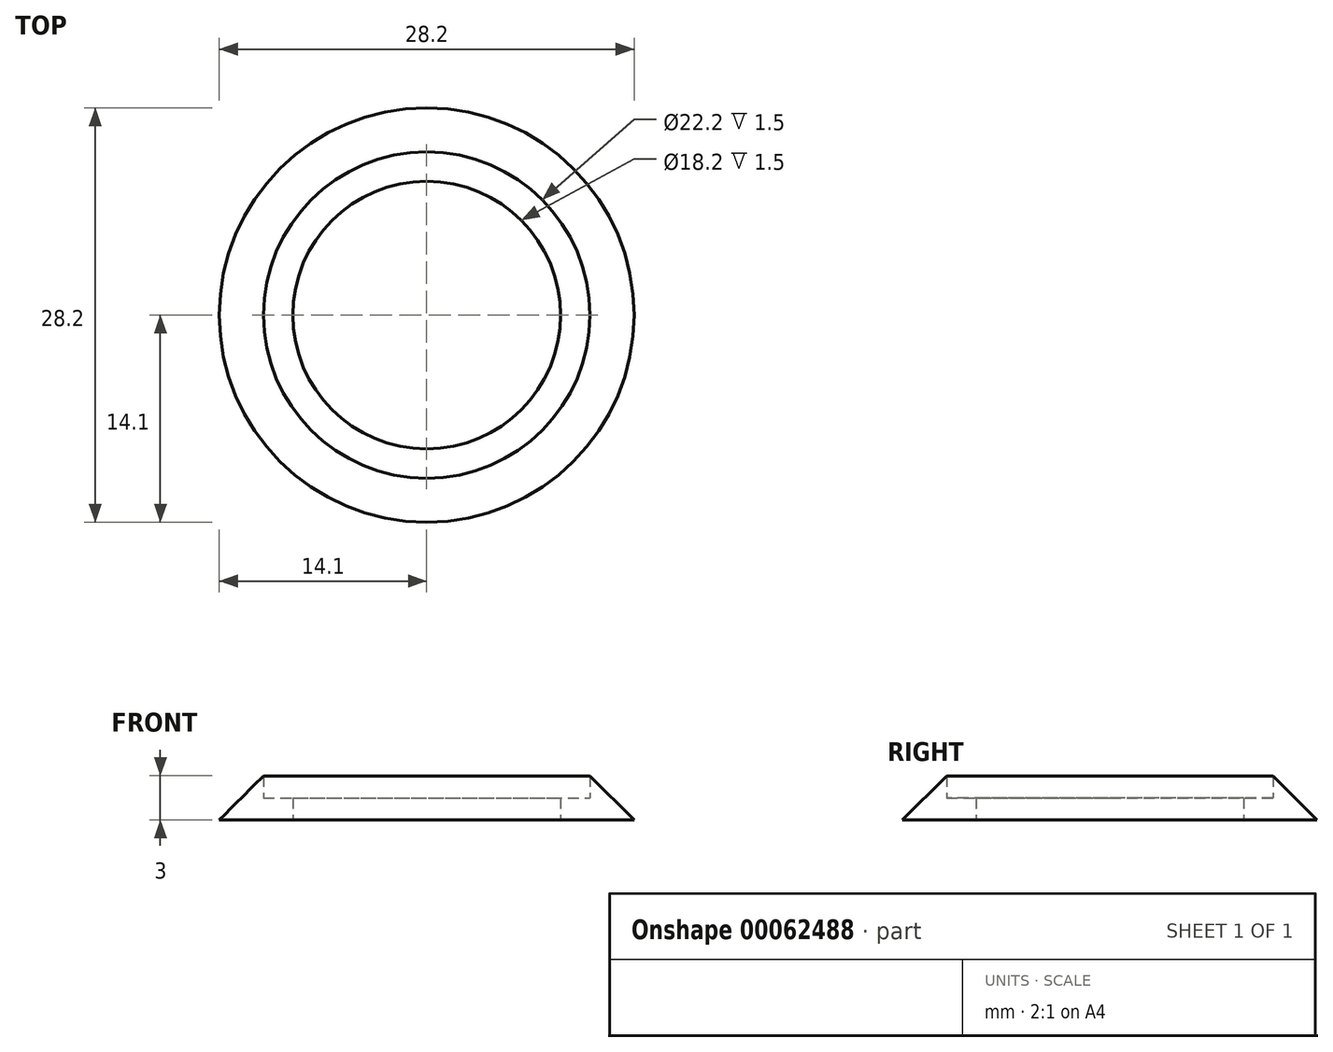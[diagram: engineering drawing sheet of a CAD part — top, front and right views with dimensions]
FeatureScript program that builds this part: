
annotation { "Feature Type Name" : "Feature", "Feature Type Description" : "" }
export const myFeature = defineFeature(function(context is Context, id is Id, definition is map)
    precondition{}
    {
        {
            var Q0;
            Q0=qCreatedBy(makeId("Front.planeOp"),FACE);
            var sketch = newSketch(context, id + "F0", { "sketchPlane" : qUnion([Q0])});
            skLineSegment(sketch, "E0", {"start": v(11.1, -3.3) * mm, "end": v(14.1, -6.3) * mm});
            skLineSegment(sketch, "E1", {"start": v(14.1, -6.3) * mm, "end": v(11.1, -6.3) * mm});
            skLineSegment(sketch, "E2", {"start": v(11.1, -6.3) * mm, "end": v(11.1, -3.3) * mm});
            skLineSegment(sketch, "E3", {"start": v(0, -3.77) * mm, "end": v(0, 4.95) * mm, "construction": true});
            skLineSegment(sketch, "E4.bottom", {"start": v(11.1, -6.3) * mm, "end": v(9.1, -6.3) * mm});
            skLineSegment(sketch, "E4.top", {"start": v(11.1, -4.8) * mm, "end": v(9.1, -4.8) * mm});
            skLineSegment(sketch, "E4.left", {"start": v(11.1, -6.3) * mm, "end": v(11.1, -4.8) * mm});
            skLineSegment(sketch, "E4.right", {"start": v(9.1, -6.3) * mm, "end": v(9.1, -4.8) * mm});
            skSolve(sketch);
        }
        {
            var Q0;
            Q0=qSketchRegion(id+"F0",true);
            var Q1;
            Q1=sQuery(id+"F0.wireOp",EDGE,"E3");
            revolve(context, id + "F1", {"entities" : qUnion([Q0]), "axis" : qUnion([Q1]), "revolveType" : RevolveType.FULL});
        }
    });
